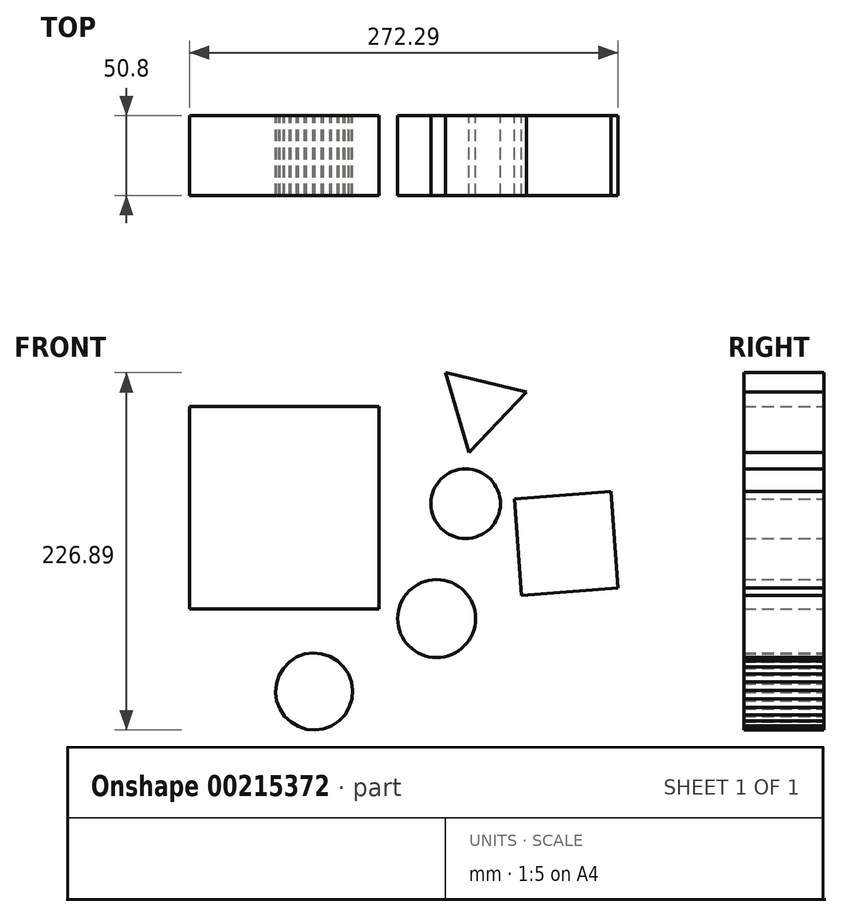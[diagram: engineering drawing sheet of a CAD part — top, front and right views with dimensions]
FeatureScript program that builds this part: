
annotation { "Feature Type Name" : "Feature", "Feature Type Description" : "" }
export const myFeature = defineFeature(function(context is Context, id is Id, definition is map)
    precondition{}
    {
        {
            var Q0;
            Q0=qCreatedBy(makeId("Front.planeOp"),FACE);
            var sketch = newSketch(context, id + "F0", { "sketchPlane" : qUnion([Q0])});
            skLineSegment(sketch, "E0.bottom", {"start": v(-12.5, -33.08) * mm, "end": v(-132.88, -33.08) * mm});
            skLineSegment(sketch, "E0.top", {"start": v(-12.5, 95.26) * mm, "end": v(-132.88, 95.26) * mm});
            skLineSegment(sketch, "E0.left", {"start": v(-12.5, -33.08) * mm, "end": v(-12.5, 95.26) * mm});
            skLineSegment(sketch, "E0.right", {"start": v(-132.88, -33.08) * mm, "end": v(-132.88, 95.26) * mm});
            skPoint(sketch, "E0.middle", {"position": v(-72.69, 31.1) * mm});
            skCircle(sketch, "E1", {"center": v(42.6, 33.65) * mm, "radius": 22.09 * mm});
            skCircle(sketch, "E2", {"center": v(24.13, -39.33) * mm, "radius": 24.77 * mm});
            skCircle(sketch, "E3.cCircle", {"center": v(-53.66, -85.6) * mm, "radius": 24.3 * mm, "construction": true});
            skLineSegment(sketch, "E3.0", {"start": v(-34.17, -100.38) * mm, "end": v(-37.95, -104.34) * mm});
            skLineSegment(sketch, "E3.1", {"start": v(-37.95, -104.34) * mm, "end": v(-42.51, -107.37) * mm});
            skLineSegment(sketch, "E3.2", {"start": v(-42.51, -107.37) * mm, "end": v(-47.63, -109.3) * mm});
            skLineSegment(sketch, "E3.3", {"start": v(-47.63, -109.3) * mm, "end": v(-53.06, -110.05) * mm});
            skLineSegment(sketch, "E3.4", {"start": v(-53.06, -110.05) * mm, "end": v(-58.51, -109.58) * mm});
            skLineSegment(sketch, "E3.5", {"start": v(-58.51, -109.58) * mm, "end": v(-63.73, -107.9) * mm});
            skLineSegment(sketch, "E3.6", {"start": v(-63.73, -107.9) * mm, "end": v(-68.43, -105.1) * mm});
            skLineSegment(sketch, "E3.7", {"start": v(-68.43, -105.1) * mm, "end": v(-72.4, -101.32) * mm});
            skLineSegment(sketch, "E3.8", {"start": v(-72.4, -101.32) * mm, "end": v(-75.43, -96.76) * mm});
            skLineSegment(sketch, "E3.9", {"start": v(-75.43, -96.76) * mm, "end": v(-77.36, -91.64) * mm});
            skLineSegment(sketch, "E3.10", {"start": v(-77.36, -91.64) * mm, "end": v(-78.11, -86.21) * mm});
            skLineSegment(sketch, "E3.11", {"start": v(-78.11, -86.21) * mm, "end": v(-77.63, -80.76) * mm});
            skLineSegment(sketch, "E3.12", {"start": v(-77.63, -80.76) * mm, "end": v(-75.95, -75.55) * mm});
            skLineSegment(sketch, "E3.13", {"start": v(-75.95, -75.55) * mm, "end": v(-73.16, -70.84) * mm});
            skLineSegment(sketch, "E3.14", {"start": v(-73.16, -70.84) * mm, "end": v(-69.38, -66.87) * mm});
            skLineSegment(sketch, "E3.15", {"start": v(-69.38, -66.87) * mm, "end": v(-64.82, -63.84) * mm});
            skLineSegment(sketch, "E3.16", {"start": v(-64.82, -63.84) * mm, "end": v(-59.7, -61.9) * mm});
            skLineSegment(sketch, "E3.17", {"start": v(-59.7, -61.9) * mm, "end": v(-54.27, -61.16) * mm});
            skLineSegment(sketch, "E3.18", {"start": v(-54.27, -61.16) * mm, "end": v(-48.81, -61.64) * mm});
            skLineSegment(sketch, "E3.19", {"start": v(-48.81, -61.64) * mm, "end": v(-43.6, -63.32) * mm});
            skLineSegment(sketch, "E3.20", {"start": v(-43.6, -63.32) * mm, "end": v(-38.9, -66.12) * mm});
            skLineSegment(sketch, "E3.21", {"start": v(-38.9, -66.12) * mm, "end": v(-34.93, -69.9) * mm});
            skLineSegment(sketch, "E3.22", {"start": v(-34.93, -69.9) * mm, "end": v(-31.9, -74.45) * mm});
            skLineSegment(sketch, "E3.23", {"start": v(-31.9, -74.45) * mm, "end": v(-29.96, -79.58) * mm});
            skLineSegment(sketch, "E3.24", {"start": v(-29.96, -79.58) * mm, "end": v(-29.22, -85) * mm});
            skLineSegment(sketch, "E3.25", {"start": v(-29.22, -85) * mm, "end": v(-29.7, -90.46) * mm});
            skLineSegment(sketch, "E3.26", {"start": v(-29.7, -90.46) * mm, "end": v(-31.37, -95.67) * mm});
            skLineSegment(sketch, "E3.27", {"start": v(-31.37, -95.67) * mm, "end": v(-34.17, -100.38) * mm});
            skPoint(sketch, "E3.0.midPoint", {"position": v(-36.06, -102.36) * mm});
            skCircle(sketch, "E4.cCircle", {"center": v(106.48, 8.38) * mm, "radius": 30.75 * mm, "construction": true});
            skLineSegment(sketch, "E4.0", {"start": v(139.41, -20.02) * mm, "end": v(78.08, -24.56) * mm});
            skLineSegment(sketch, "E4.1", {"start": v(78.08, -24.56) * mm, "end": v(73.54, 36.77) * mm});
            skLineSegment(sketch, "E4.2", {"start": v(73.54, 36.77) * mm, "end": v(134.87, 41.31) * mm});
            skLineSegment(sketch, "E4.3", {"start": v(134.87, 41.31) * mm, "end": v(139.41, -20.02) * mm});
            skPoint(sketch, "E4.0.midPoint", {"position": v(108.75, -22.29) * mm});
            skCircle(sketch, "E5.cCircle", {"center": v(51.96, 95.83) * mm, "radius": 15.26 * mm, "construction": true});
            skLineSegment(sketch, "E5.0", {"start": v(81.23, 104.5) * mm, "end": v(44.84, 66.14) * mm});
            skLineSegment(sketch, "E5.1", {"start": v(44.84, 66.14) * mm, "end": v(29.81, 116.84) * mm});
            skLineSegment(sketch, "E5.2", {"start": v(29.81, 116.84) * mm, "end": v(81.23, 104.5) * mm});
            skPoint(sketch, "E5.0.midPoint", {"position": v(63.03, 85.32) * mm});
            skSolve(sketch);
        }
        {
            var Q0;
            Q0 = qSketchRegion(id + "F0", true);
            extrude(context, id + "F1", {"entities" : qUnion([Q0]), "depth" : 25.4 * mm});
        }
        {
            var Q0;
            Q0 = qSketchRegion(id + "F0", true);
            extrude(context, id + "F2", {"entities" : qUnion([Q0]), "operationType" : NewBodyOperationType.ADD, "oppositeDirection" : true, "depth" : 25.4 * mm});
        }
    });
